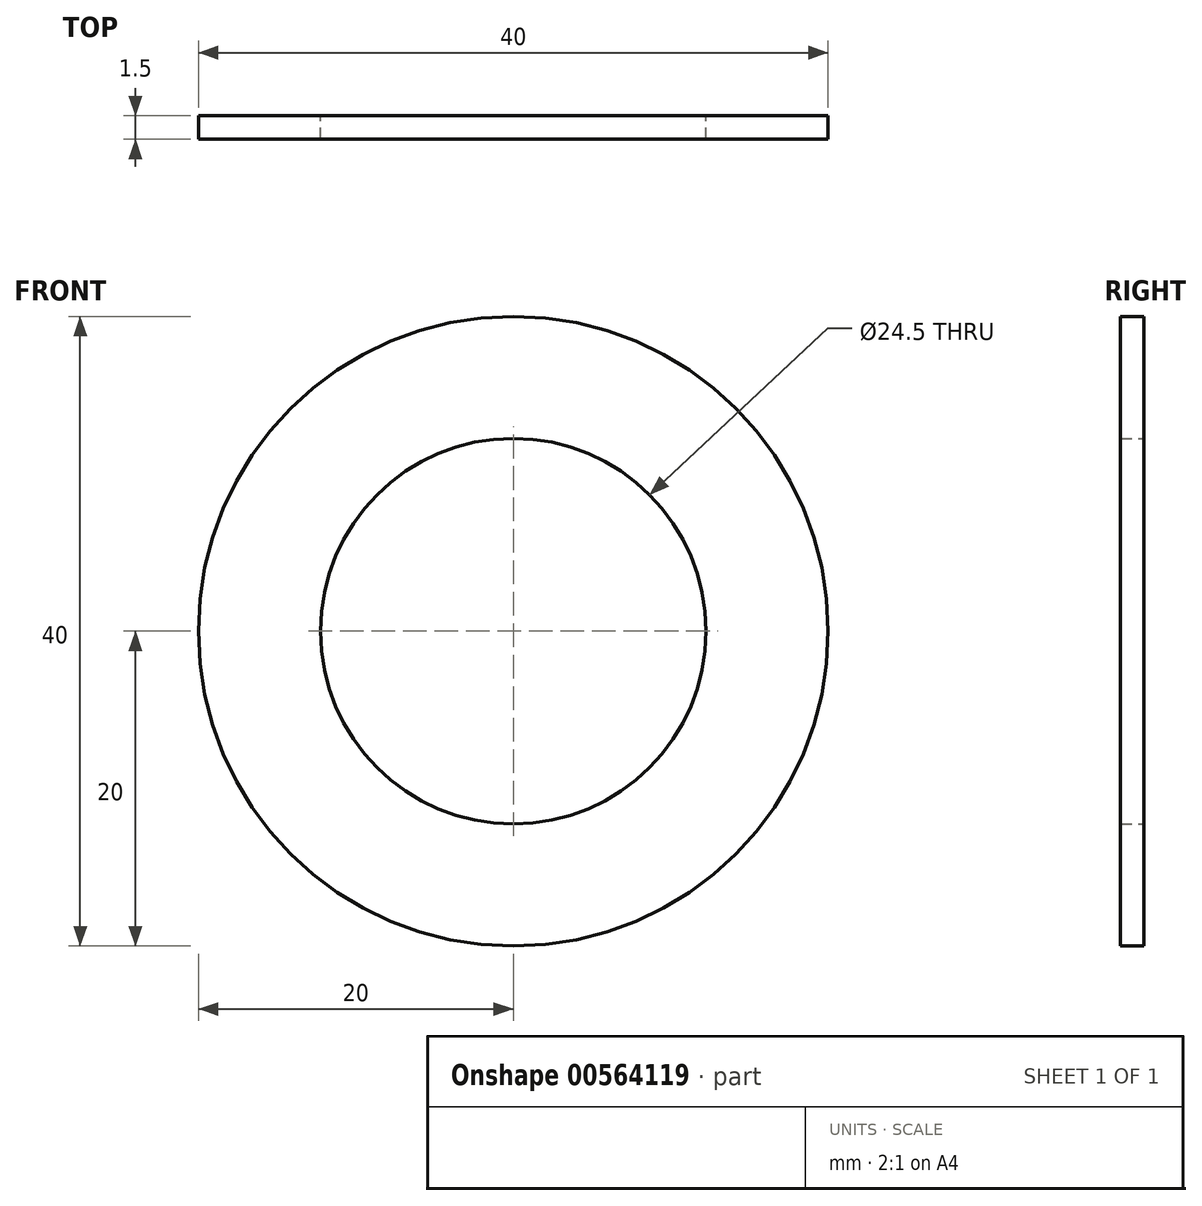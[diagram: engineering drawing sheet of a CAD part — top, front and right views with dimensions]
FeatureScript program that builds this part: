
annotation { "Feature Type Name" : "Feature", "Feature Type Description" : "" }
export const myFeature = defineFeature(function(context is Context, id is Id, definition is map)
    precondition{}
    {
        {
            var Q0;
            Q0=qCreatedBy(makeId("Front.planeOp"),FACE);
            var sketch = newSketch(context, id + "F0", { "sketchPlane" : qUnion([Q0])});
            skCircle(sketch, "E0", {"center": v(0, 0) * mm, "radius": 12.25 * mm});
            skCircle(sketch, "E1", {"center": v(0, 0) * mm, "radius": 20 * mm});
            skSolve(sketch);
        }
        {
            var Q0;
            Q0 = qSketchRegion(id + "F0", true);
            extrude(context, id + "F1", {"entities" : qUnion([Q0]), "depth" : 1.5 * mm, "offsetDistance" : 25.4 * mm});
        }
    });
